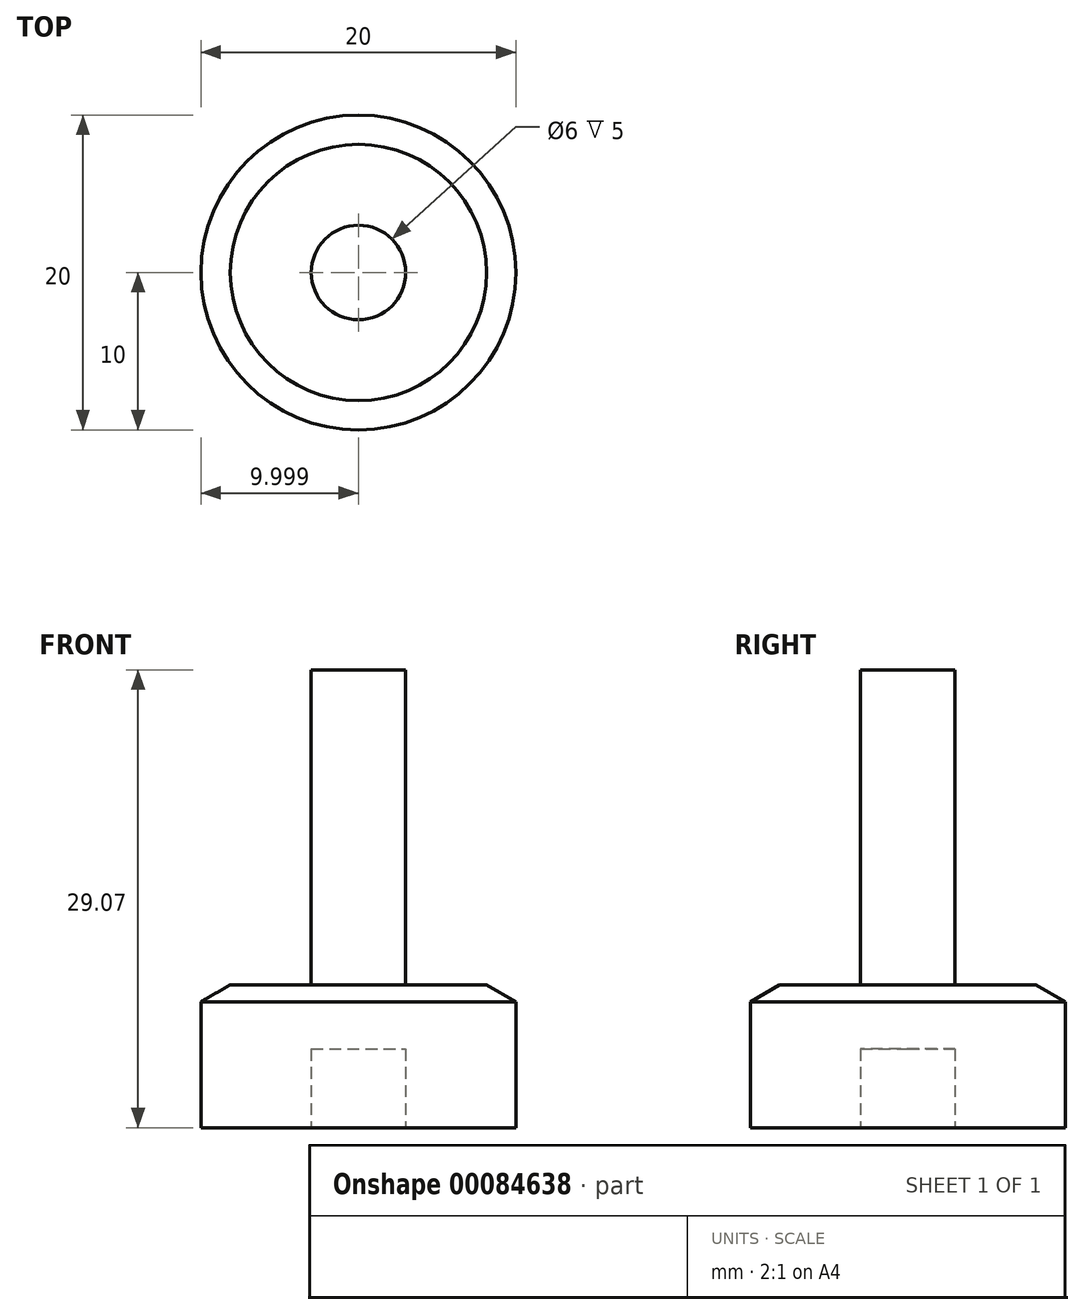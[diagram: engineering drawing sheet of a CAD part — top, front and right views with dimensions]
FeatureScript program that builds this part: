
annotation { "Feature Type Name" : "Feature", "Feature Type Description" : "" }
export const myFeature = defineFeature(function(context is Context, id is Id, definition is map)
    precondition{}
    {
        {
            var Q0;
            Q0=qCreatedBy(makeId("Front.planeOp"),FACE);
            var sketch = newSketch(context, id + "F0", { "sketchPlane" : qUnion([Q0])});
            skLineSegment(sketch, "E0.bottom", {"start": v(-30.55, 8) * mm, "end": v(-20.55, 8) * mm});
            skLineSegment(sketch, "E0.top", {"start": v(-30.55, 0) * mm, "end": v(-23.55, 0) * mm});
            skLineSegment(sketch, "E0.left", {"start": v(-30.55, 8) * mm, "end": v(-30.55, 0) * mm});
            skPoint(sketch, "E1", {"position": v(-20.55, 8) * mm});
            skPoint(sketch, "E2", {"position": v(-20.55, 0) * mm});
            skPoint(sketch, "E3", {"position": v(-20.55, 9.07) * mm});
            skLineSegment(sketch, "E4", {"start": v(-20.55, 8) * mm, "end": v(-20.55, 9.07) * mm});
            skLineSegment(sketch, "E5", {"start": v(-30.55, 8) * mm, "end": v(-28.7, 9.07) * mm});
            skLineSegment(sketch, "E6", {"start": v(-28.7, 9.07) * mm, "end": v(-20.55, 9.07) * mm});
            skLineSegment(sketch, "E7", {"start": v(-20.55, 8) * mm, "end": v(-20.55, 5) * mm});
            skPoint(sketch, "E0.right.end.orphan", {"position": v(-10.55, 0) * mm});
            skPoint(sketch, "E8.start.orphan", {"position": v(-10.55, 8) * mm});
            skLineSegment(sketch, "E9", {"start": v(-20.55, 9.07) * mm, "end": v(-20.55, 29.07) * mm});
            skLineSegment(sketch, "E10", {"start": v(-20.55, 29.07) * mm, "end": v(-23.55, 29.07) * mm});
            skLineSegment(sketch, "E11", {"start": v(-23.55, 29.07) * mm, "end": v(-23.55, 0) * mm});
            skPoint(sketch, "E12.start.orphan", {"position": v(-20.55, 4) * mm});
            skLineSegment(sketch, "E13", {"start": v(-20.55, 5) * mm, "end": v(-23.55, 5) * mm});
            skPoint(sketch, "E14", {"position": v(-20.55, 5) * mm});
            skSolve(sketch);
        }
        {
            var Q0;
            {var subQ0=sQuery(id+"F0.wireOp",EDGE,"E9");Q0=makeQuery(id+"F0.imprint","IMPRINT",FACE,{"disambiguationData":[TD([[makeQuery(id+"F0.imprint","IMPRINT",EDGE,{"derivedFrom":subQ0}),1.0]])]});}
            var Q1;
            {var subQ5=sQuery(id+"F0.wireOp",EDGE,"E0.top");Q1=makeQuery(id+"F0.imprint","IMPRINT",FACE,{"disambiguationData":[TD([[makeQuery(id+"F0.imprint","IMPRINT",EDGE,{"derivedFrom":subQ5}),1.0]])]});}
            var Q2;
            {var subQ0=sQuery(id+"F0.wireOp",EDGE,"E5");Q2=makeQuery(id+"F0.imprint","IMPRINT",FACE,{"disambiguationData":[TD([[makeQuery(id+"F0.imprint","IMPRINT",EDGE,{"derivedFrom":subQ0}),-1.0]])]});}
            var Q3;
            {var subQ0=sQuery(id+"F0.wireOp",EDGE,"E7");Q3=makeQuery(id+"F0.imprint","IMPRINT",FACE,{"disambiguationData":[TD([[makeQuery(id+"F0.imprint","IMPRINT",EDGE,{"derivedFrom":subQ0}),-1.0]])]});}
            var Q4;
            {var subQ0=sQuery(id+"F0.wireOp",EDGE,"E4");Q4=makeQuery(id+"F0.imprint","IMPRINT",FACE,{"disambiguationData":[TD([[makeQuery(id+"F0.imprint","IMPRINT",EDGE,{"derivedFrom":subQ0}),1.0]])]});}
            var Q5;
            Q5=sQuery(id+"F0.wireOp",EDGE,"E9");
            revolve(context, id + "F1", {"entities" : qUnion([Q0, Q1, Q2, Q3, Q4]), "axis" : qUnion([Q5]), "revolveType" : RevolveType.FULL});
        }
    });
